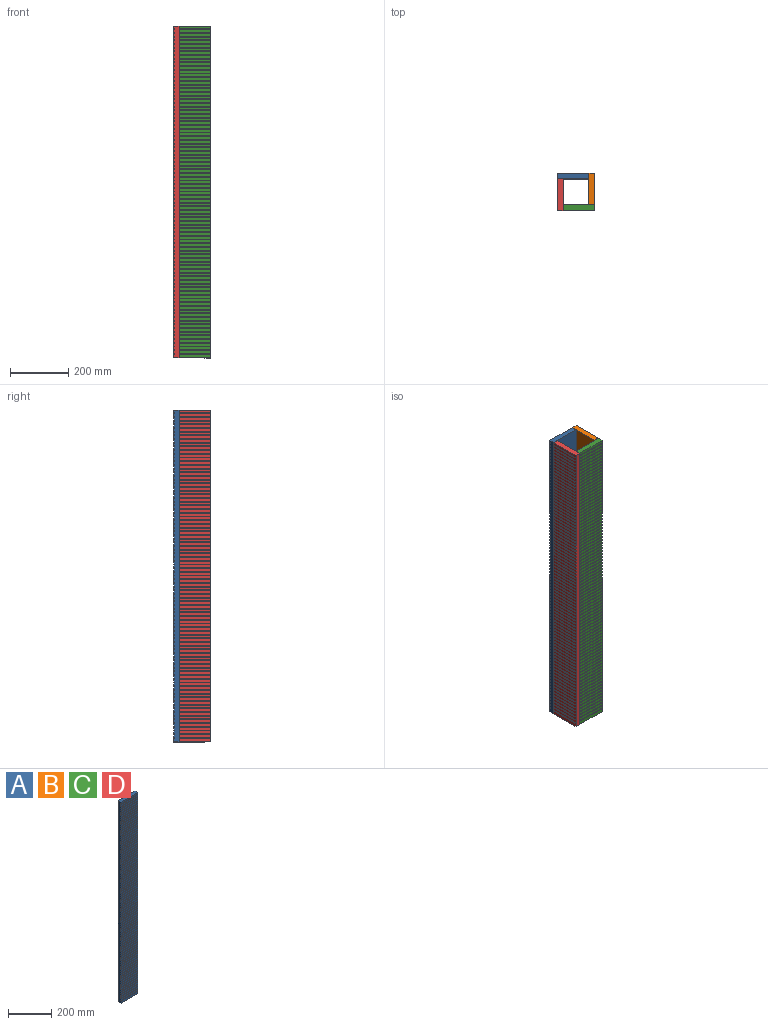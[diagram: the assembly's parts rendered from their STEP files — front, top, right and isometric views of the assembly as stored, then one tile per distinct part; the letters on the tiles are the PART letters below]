
ASSEMBLY  parts=4 mates=3
PART A: 362 faces, bbox 108x19.1x1143 mm
  f0: plane 1143x19.05mm, normal (-1,0,0), area 21325.6mm2, adj f1,f2,f3,f4,f5,f6,f7,f8
  f1: plane 107.95x9.53mm, normal (0,-1,0), area 1028.2mm2, adj f0,f90,f93,f359
  f2: plane 107.95x9.53mm, normal (0,-1,0), area 1028.2mm2, adj f0,f90,f356,f360
  f3: plane 107.95x9.53mm, normal (0,-1,0), area 1028.2mm2, adj f0,f90,f353,f357
  f4: plane 107.95x9.53mm, normal (0,-1,0), area 1028.2mm2, adj f0,f90,f350,f354
  f5: plane 107.95x9.53mm, normal (0,-1,0), area 1028.2mm2, adj f0,f90,f347,f351
  f6: plane 107.95x9.53mm, normal (0,-1,0), area 1028.2mm2, adj f0,f90,f344,f348
  f7: plane 107.95x9.53mm, normal (0,-1,0), area 1028.2mm2, adj f0,f90,f341,f345
  f8: plane 107.95x9.53mm, normal (0,-1,0), area 1028.2mm2, adj f0,f90,f338,f342
  f9: plane 107.95x9.53mm, normal (0,-1,0), area 1028.2mm2, adj f0,f90,f335,f339
  f10: plane 107.95x9.53mm, normal (0,-1,0), area 1028.2mm2, adj f0,f90,f332,f336
  f11: plane 107.95x9.53mm, normal (0,-1,0), area 1028.2mm2, adj f0,f90,f329,f333
  f12: plane 107.95x9.53mm, normal (0,-1,0), area 1028.2mm2, adj f0,f90,f326,f330
  f13: plane 107.95x9.53mm, normal (0,-1,0), area 1028.2mm2, adj f0,f90,f323,f327
  f14: plane 107.95x9.53mm, normal (0,-1,0), area 1028.2mm2, adj f0,f90,f320,f324
  f15: plane 107.95x9.53mm, normal (0,-1,0), area 1028.2mm2, adj f0,f90,f317,f321
  f16: plane 107.95x9.53mm, normal (0,-1,0), area 1028.2mm2, adj f0,f90,f314,f318
  f17: plane 107.95x9.53mm, normal (0,-1,0), area 1028.2mm2, adj f0,f90,f311,f315
  f18: plane 107.95x9.53mm, normal (0,-1,0), area 1028.2mm2, adj f0,f90,f308,f312
  f19: plane 107.95x9.53mm, normal (0,-1,0), area 1028.2mm2, adj f0,f90,f305,f309
  f20: plane 107.95x9.53mm, normal (0,-1,0), area 1028.2mm2, adj f0,f90,f302,f306
  f21: plane 107.95x9.53mm, normal (0,-1,0), area 1028.2mm2, adj f0,f90,f299,f303
  f22: plane 107.95x9.53mm, normal (0,-1,0), area 1028.2mm2, adj f0,f90,f296,f300
  f23: plane 107.95x9.53mm, normal (0,-1,0), area 1028.2mm2, adj f0,f90,f293,f297
  f24: plane 107.95x9.53mm, normal (0,-1,0), area 1028.2mm2, adj f0,f90,f290,f294
  f25: plane 107.95x9.53mm, normal (0,-1,0), area 1028.2mm2, adj f0,f90,f287,f291
  f26: plane 107.95x9.53mm, normal (0,-1,0), area 1028.2mm2, adj f0,f90,f284,f288
  f27: plane 107.95x9.53mm, normal (0,-1,0), area 1028.2mm2, adj f0,f90,f281,f285
  f28: plane 107.95x9.53mm, normal (0,-1,0), area 1028.2mm2, adj f0,f90,f278,f282
  f29: plane 107.95x9.53mm, normal (0,-1,0), area 1028.2mm2, adj f0,f90,f275,f279
  f30: plane 107.95x9.53mm, normal (0,-1,0), area 1028.2mm2, adj f0,f90,f272,f276
  f31: plane 107.95x9.53mm, normal (0,-1,0), area 1028.2mm2, adj f0,f90,f269,f273
  f32: plane 107.95x9.53mm, normal (0,-1,0), area 1028.2mm2, adj f0,f90,f266,f270
  f33: plane 107.95x9.53mm, normal (0,-1,0), area 1028.2mm2, adj f0,f90,f263,f267
  f34: plane 107.95x9.53mm, normal (0,-1,0), area 1028.2mm2, adj f0,f90,f260,f264
  f35: plane 107.95x9.53mm, normal (0,-1,0), area 1028.2mm2, adj f0,f90,f257,f261
  f36: plane 107.95x9.53mm, normal (0,-1,0), area 1028.2mm2, adj f0,f90,f254,f258
  f37: plane 107.95x9.53mm, normal (0,-1,0), area 1028.2mm2, adj f0,f90,f251,f255
  f38: plane 107.95x9.53mm, normal (0,-1,0), area 1028.2mm2, adj f0,f90,f248,f252
  f39: plane 107.95x9.53mm, normal (0,-1,0), area 1028.2mm2, adj f0,f90,f245,f249
  f40: plane 107.95x9.53mm, normal (0,-1,0), area 1028.2mm2, adj f0,f90,f242,f246
  f41: plane 107.95x9.53mm, normal (0,-1,0), area 1028.2mm2, adj f0,f90,f239,f243
  f42: plane 107.95x9.53mm, normal (0,-1,0), area 1028.2mm2, adj f0,f90,f236,f240
  f43: plane 107.95x9.53mm, normal (0,-1,0), area 1028.2mm2, adj f0,f90,f233,f237
  f44: plane 107.95x9.53mm, normal (0,-1,0), area 1028.2mm2, adj f0,f90,f230,f234
  f45: plane 107.95x9.53mm, normal (0,-1,0), area 1028.2mm2, adj f0,f90,f227,f231
  f46: plane 107.95x9.53mm, normal (0,-1,0), area 1028.2mm2, adj f0,f90,f224,f228
  f47: plane 107.95x9.53mm, normal (0,-1,0), area 1028.2mm2, adj f0,f90,f221,f225
  f48: plane 107.95x9.53mm, normal (0,-1,0), area 1028.2mm2, adj f0,f90,f218,f222
  f49: plane 107.95x9.53mm, normal (0,-1,0), area 1028.2mm2, adj f0,f90,f215,f219
  f50: plane 107.95x9.53mm, normal (0,-1,0), area 1028.2mm2, adj f0,f90,f212,f216
  f51: plane 107.95x9.53mm, normal (0,-1,0), area 1028.2mm2, adj f0,f90,f209,f213
  f52: plane 107.95x9.53mm, normal (0,-1,0), area 1028.2mm2, adj f0,f90,f206,f210
  f53: plane 107.95x9.53mm, normal (0,-1,0), area 1028.2mm2, adj f0,f90,f203,f207
  f54: plane 107.95x9.53mm, normal (0,-1,0), area 1028.2mm2, adj f0,f90,f200,f204
  f55: plane 107.95x9.53mm, normal (0,-1,0), area 1028.2mm2, adj f0,f90,f197,f201
  f56: plane 107.95x9.53mm, normal (0,-1,0), area 1028.2mm2, adj f0,f90,f194,f198
  f57: plane 107.95x9.53mm, normal (0,-1,0), area 1028.2mm2, adj f0,f90,f191,f195
  f58: plane 107.95x9.53mm, normal (0,-1,0), area 1028.2mm2, adj f0,f90,f188,f192
  f59: plane 107.95x9.53mm, normal (0,-1,0), area 1028.2mm2, adj f0,f90,f185,f189
  f60: plane 107.95x9.53mm, normal (0,-1,0), area 1028.2mm2, adj f0,f90,f182,f186
  f61: plane 107.95x9.53mm, normal (0,-1,0), area 1028.2mm2, adj f0,f90,f179,f183
  f62: plane 107.95x9.53mm, normal (0,-1,0), area 1028.2mm2, adj f0,f90,f176,f180
  f63: plane 107.95x9.53mm, normal (0,-1,0), area 1028.2mm2, adj f0,f90,f173,f177
  f64: plane 107.95x9.53mm, normal (0,-1,0), area 1028.2mm2, adj f0,f90,f170,f174
  f65: plane 107.95x9.53mm, normal (0,-1,0), area 1028.2mm2, adj f0,f90,f167,f171
  f66: plane 107.95x9.53mm, normal (0,-1,0), area 1028.2mm2, adj f0,f90,f164,f168
  f67: plane 107.95x9.53mm, normal (0,-1,0), area 1028.2mm2, adj f0,f90,f161,f165
  f68: plane 107.95x9.53mm, normal (0,-1,0), area 1028.2mm2, adj f0,f90,f158,f162
  f69: plane 107.95x9.53mm, normal (0,-1,0), area 1028.2mm2, adj f0,f90,f155,f159
  f70: plane 107.95x9.53mm, normal (0,-1,0), area 1028.2mm2, adj f0,f90,f152,f156
  f71: plane 107.95x9.53mm, normal (0,-1,0), area 1028.2mm2, adj f0,f90,f149,f153
  f72: plane 107.95x9.53mm, normal (0,-1,0), area 1028.2mm2, adj f0,f90,f146,f150
  f73: plane 107.95x9.53mm, normal (0,-1,0), area 1028.2mm2, adj f0,f90,f143,f147
  f74: plane 107.95x9.53mm, normal (0,-1,0), area 1028.2mm2, adj f0,f90,f140,f144
  f75: plane 107.95x9.53mm, normal (0,-1,0), area 1028.2mm2, adj f0,f90,f137,f141
  f76: plane 107.95x9.53mm, normal (0,-1,0), area 1028.2mm2, adj f0,f90,f134,f138
  f77: plane 107.95x9.53mm, normal (0,-1,0), area 1028.2mm2, adj f0,f90,f131,f135
  f78: plane 107.95x9.53mm, normal (0,-1,0), area 1028.2mm2, adj f0,f90,f128,f132
  f79: plane 107.95x9.53mm, normal (0,-1,0), area 1028.2mm2, adj f0,f90,f125,f129
  f80: plane 107.95x9.53mm, normal (0,-1,0), area 1028.2mm2, adj f0,f90,f122,f126
  f81: plane 107.95x9.53mm, normal (0,-1,0), area 1028.2mm2, adj f0,f90,f119,f123
  f82: plane 107.95x9.53mm, normal (0,-1,0), area 1028.2mm2, adj f0,f90,f116,f120
  f83: plane 107.95x9.53mm, normal (0,-1,0), area 1028.2mm2, adj f0,f90,f113,f117
  f84: plane 107.95x9.53mm, normal (0,-1,0), area 1028.2mm2, adj f0,f90,f110,f114
  f85: plane 107.95x9.53mm, normal (0,-1,0), area 1028.2mm2, adj f0,f90,f107,f111
  f86: plane 107.95x9.53mm, normal (0,-1,0), area 1028.2mm2, adj f0,f90,f104,f108
  f87: plane 107.95x9.53mm, normal (0,-1,0), area 1028.2mm2, adj f0,f90,f101,f105
  f88: plane 107.95x9.53mm, normal (0,-1,0), area 1028.2mm2, adj f0,f90,f98,f102
  f89: plane 107.95x9.53mm, normal (0,-1,0), area 1028.2mm2, adj f0,f90,f95,f99
  f90: plane 1143x19.05mm, normal (1,0,0), area 21325.6mm2, adj f1,f2,f3,f4,f5,f6,f7,f8
  f91: plane 1143x107.95mm, normal (0,1,0), area 123386.8mm2, adj f0,f90,f93,f94
  f92: plane 107.95x12.7mm, normal (0,-1,0), area 1371mm2, adj f0,f90,f94,f96
  f93: plane 107.95x19.05mm, normal (0,0,1), area 2056.4mm2, adj f0,f1,f90,f91
  f94: plane 107.95x19.05mm, normal (0,0,-1), area 2056.4mm2, adj f0,f90,f91,f92
  f95: plane 107.95x1.59mm, normal (0,0,-1), area 171.4mm2, adj f0,f89,f90,f97
  f96: plane 107.95x1.59mm, normal (0,0,1), area 171.4mm2, adj f0,f90,f92,f97
  f97: plane 107.95x3.18mm, normal (0,-1,0), area 342.7mm2, adj f0,f90,f95,f96
  f98: plane 107.95x1.59mm, normal (0,0,-1), area 171.4mm2, adj f0,f88,f90,f100
  f99: plane 107.95x1.59mm, normal (0,0,1), area 171.4mm2, adj f0,f89,f90,f100
  f100: plane 107.95x3.18mm, normal (0,-1,0), area 342.7mm2, adj f0,f90,f98,f99
  f101: plane 107.95x1.59mm, normal (0,0,-1), area 171.4mm2, adj f0,f87,f90,f103
  f102: plane 107.95x1.59mm, normal (0,0,1), area 171.4mm2, adj f0,f88,f90,f103
  f103: plane 107.95x3.18mm, normal (0,-1,0), area 342.7mm2, adj f0,f90,f101,f102
  f104: plane 107.95x1.59mm, normal (0,0,-1), area 171.4mm2, adj f0,f86,f90,f106
  f105: plane 107.95x1.59mm, normal (0,0,1), area 171.4mm2, adj f0,f87,f90,f106
  f106: plane 107.95x3.18mm, normal (0,-1,0), area 342.7mm2, adj f0,f90,f104,f105
  f107: plane 107.95x1.59mm, normal (0,0,-1), area 171.4mm2, adj f0,f85,f90,f109
  f108: plane 107.95x1.59mm, normal (0,0,1), area 171.4mm2, adj f0,f86,f90,f109
  f109: plane 107.95x3.18mm, normal (0,-1,0), area 342.7mm2, adj f0,f90,f107,f108
  f110: plane 107.95x1.59mm, normal (0,0,-1), area 171.4mm2, adj f0,f84,f90,f112
  f111: plane 107.95x1.59mm, normal (0,0,1), area 171.4mm2, adj f0,f85,f90,f112
  f112: plane 107.95x3.18mm, normal (0,-1,0), area 342.7mm2, adj f0,f90,f110,f111
  f113: plane 107.95x1.59mm, normal (0,0,-1), area 171.4mm2, adj f0,f83,f90,f115
  f114: plane 107.95x1.59mm, normal (0,0,1), area 171.4mm2, adj f0,f84,f90,f115
  f115: plane 107.95x3.18mm, normal (0,-1,0), area 342.7mm2, adj f0,f90,f113,f114
  f116: plane 107.95x1.59mm, normal (0,0,-1), area 171.4mm2, adj f0,f82,f90,f118
  f117: plane 107.95x1.59mm, normal (0,0,1), area 171.4mm2, adj f0,f83,f90,f118
  f118: plane 107.95x3.18mm, normal (0,-1,0), area 342.7mm2, adj f0,f90,f116,f117
  f119: plane 107.95x1.59mm, normal (0,0,-1), area 171.4mm2, adj f0,f81,f90,f121
  f120: plane 107.95x1.59mm, normal (0,0,1), area 171.4mm2, adj f0,f82,f90,f121
  f121: plane 107.95x3.18mm, normal (0,-1,0), area 342.7mm2, adj f0,f90,f119,f120
  f122: plane 107.95x1.59mm, normal (0,0,-1), area 171.4mm2, adj f0,f80,f90,f124
  f123: plane 107.95x1.59mm, normal (0,0,1), area 171.4mm2, adj f0,f81,f90,f124
  f124: plane 107.95x3.18mm, normal (0,-1,0), area 342.7mm2, adj f0,f90,f122,f123
  f125: plane 107.95x1.59mm, normal (0,0,-1), area 171.4mm2, adj f0,f79,f90,f127
  f126: plane 107.95x1.59mm, normal (0,0,1), area 171.4mm2, adj f0,f80,f90,f127
  f127: plane 107.95x3.18mm, normal (0,-1,0), area 342.7mm2, adj f0,f90,f125,f126
  f128: plane 107.95x1.59mm, normal (0,0,-1), area 171.4mm2, adj f0,f78,f90,f130
  f129: plane 107.95x1.59mm, normal (0,0,1), area 171.4mm2, adj f0,f79,f90,f130
  f130: plane 107.95x3.18mm, normal (0,-1,0), area 342.7mm2, adj f0,f90,f128,f129
  f131: plane 107.95x1.59mm, normal (0,0,-1), area 171.4mm2, adj f0,f77,f90,f133
  f132: plane 107.95x1.59mm, normal (0,0,1), area 171.4mm2, adj f0,f78,f90,f133
  f133: plane 107.95x3.18mm, normal (0,-1,0), area 342.7mm2, adj f0,f90,f131,f132
  f134: plane 107.95x1.59mm, normal (0,0,-1), area 171.4mm2, adj f0,f76,f90,f136
  f135: plane 107.95x1.59mm, normal (0,0,1), area 171.4mm2, adj f0,f77,f90,f136
  f136: plane 107.95x3.18mm, normal (0,-1,0), area 342.7mm2, adj f0,f90,f134,f135
  f137: plane 107.95x1.59mm, normal (0,0,-1), area 171.4mm2, adj f0,f75,f90,f139
  f138: plane 107.95x1.59mm, normal (0,0,1), area 171.4mm2, adj f0,f76,f90,f139
  f139: plane 107.95x3.18mm, normal (0,-1,0), area 342.7mm2, adj f0,f90,f137,f138
  f140: plane 107.95x1.59mm, normal (0,0,-1), area 171.4mm2, adj f0,f74,f90,f142
  f141: plane 107.95x1.59mm, normal (0,0,1), area 171.4mm2, adj f0,f75,f90,f142
  f142: plane 107.95x3.18mm, normal (0,-1,0), area 342.7mm2, adj f0,f90,f140,f141
  f143: plane 107.95x1.59mm, normal (0,0,-1), area 171.4mm2, adj f0,f73,f90,f145
  f144: plane 107.95x1.59mm, normal (0,0,1), area 171.4mm2, adj f0,f74,f90,f145
  f145: plane 107.95x3.18mm, normal (0,-1,0), area 342.7mm2, adj f0,f90,f143,f144
  f146: plane 107.95x1.59mm, normal (0,0,-1), area 171.4mm2, adj f0,f72,f90,f148
  f147: plane 107.95x1.59mm, normal (0,0,1), area 171.4mm2, adj f0,f73,f90,f148
  f148: plane 107.95x3.18mm, normal (0,-1,0), area 342.7mm2, adj f0,f90,f146,f147
  f149: plane 107.95x1.59mm, normal (0,0,-1), area 171.4mm2, adj f0,f71,f90,f151
  f150: plane 107.95x1.59mm, normal (0,0,1), area 171.4mm2, adj f0,f72,f90,f151
  f151: plane 107.95x3.18mm, normal (0,-1,0), area 342.7mm2, adj f0,f90,f149,f150
  f152: plane 107.95x1.59mm, normal (0,0,-1), area 171.4mm2, adj f0,f70,f90,f154
  f153: plane 107.95x1.59mm, normal (0,0,1), area 171.4mm2, adj f0,f71,f90,f154
  f154: plane 107.95x3.18mm, normal (0,-1,0), area 342.7mm2, adj f0,f90,f152,f153
  f155: plane 107.95x1.59mm, normal (0,0,-1), area 171.4mm2, adj f0,f69,f90,f157
  f156: plane 107.95x1.59mm, normal (0,0,1), area 171.4mm2, adj f0,f70,f90,f157
  f157: plane 107.95x3.18mm, normal (0,-1,0), area 342.7mm2, adj f0,f90,f155,f156
  f158: plane 107.95x1.59mm, normal (0,0,-1), area 171.4mm2, adj f0,f68,f90,f160
  f159: plane 107.95x1.59mm, normal (0,0,1), area 171.4mm2, adj f0,f69,f90,f160
  f160: plane 107.95x3.18mm, normal (0,-1,0), area 342.7mm2, adj f0,f90,f158,f159
  f161: plane 107.95x1.59mm, normal (0,0,-1), area 171.4mm2, adj f0,f67,f90,f163
  f162: plane 107.95x1.59mm, normal (0,0,1), area 171.4mm2, adj f0,f68,f90,f163
  f163: plane 107.95x3.18mm, normal (0,-1,0), area 342.7mm2, adj f0,f90,f161,f162
  f164: plane 107.95x1.59mm, normal (0,0,-1), area 171.4mm2, adj f0,f66,f90,f166
  f165: plane 107.95x1.59mm, normal (0,0,1), area 171.4mm2, adj f0,f67,f90,f166
  f166: plane 107.95x3.18mm, normal (0,-1,0), area 342.7mm2, adj f0,f90,f164,f165
  f167: plane 107.95x1.59mm, normal (0,0,-1), area 171.4mm2, adj f0,f65,f90,f169
  f168: plane 107.95x1.59mm, normal (0,0,1), area 171.4mm2, adj f0,f66,f90,f169
  f169: plane 107.95x3.18mm, normal (0,-1,0), area 342.7mm2, adj f0,f90,f167,f168
  f170: plane 107.95x1.59mm, normal (0,0,-1), area 171.4mm2, adj f0,f64,f90,f172
  f171: plane 107.95x1.59mm, normal (0,0,1), area 171.4mm2, adj f0,f65,f90,f172
  f172: plane 107.95x3.18mm, normal (0,-1,0), area 342.7mm2, adj f0,f90,f170,f171
  f173: plane 107.95x1.59mm, normal (0,0,-1), area 171.4mm2, adj f0,f63,f90,f175
  f174: plane 107.95x1.59mm, normal (0,0,1), area 171.4mm2, adj f0,f64,f90,f175
  f175: plane 107.95x3.18mm, normal (0,-1,0), area 342.7mm2, adj f0,f90,f173,f174
  f176: plane 107.95x1.59mm, normal (0,0,-1), area 171.4mm2, adj f0,f62,f90,f178
  f177: plane 107.95x1.59mm, normal (0,0,1), area 171.4mm2, adj f0,f63,f90,f178
  f178: plane 107.95x3.18mm, normal (0,-1,0), area 342.7mm2, adj f0,f90,f176,f177
  f179: plane 107.95x1.59mm, normal (0,0,-1), area 171.4mm2, adj f0,f61,f90,f181
  f180: plane 107.95x1.59mm, normal (0,0,1), area 171.4mm2, adj f0,f62,f90,f181
  f181: plane 107.95x3.18mm, normal (0,-1,0), area 342.7mm2, adj f0,f90,f179,f180
  f182: plane 107.95x1.59mm, normal (0,0,-1), area 171.4mm2, adj f0,f60,f90,f184
  f183: plane 107.95x1.59mm, normal (0,0,1), area 171.4mm2, adj f0,f61,f90,f184
  f184: plane 107.95x3.18mm, normal (0,-1,0), area 342.7mm2, adj f0,f90,f182,f183
  f185: plane 107.95x1.59mm, normal (0,0,-1), area 171.4mm2, adj f0,f59,f90,f187
  f186: plane 107.95x1.59mm, normal (0,0,1), area 171.4mm2, adj f0,f60,f90,f187
  f187: plane 107.95x3.18mm, normal (0,-1,0), area 342.7mm2, adj f0,f90,f185,f186
  f188: plane 107.95x1.59mm, normal (0,0,-1), area 171.4mm2, adj f0,f58,f90,f190
  f189: plane 107.95x1.59mm, normal (0,0,1), area 171.4mm2, adj f0,f59,f90,f190
  f190: plane 107.95x3.18mm, normal (0,-1,0), area 342.7mm2, adj f0,f90,f188,f189
  f191: plane 107.95x1.59mm, normal (0,0,-1), area 171.4mm2, adj f0,f57,f90,f193
  f192: plane 107.95x1.59mm, normal (0,0,1), area 171.4mm2, adj f0,f58,f90,f193
  f193: plane 107.95x3.18mm, normal (0,-1,0), area 342.7mm2, adj f0,f90,f191,f192
  f194: plane 107.95x1.59mm, normal (0,0,-1), area 171.4mm2, adj f0,f56,f90,f196
  f195: plane 107.95x1.59mm, normal (0,0,1), area 171.4mm2, adj f0,f57,f90,f196
  f196: plane 107.95x3.18mm, normal (0,-1,0), area 342.7mm2, adj f0,f90,f194,f195
  f197: plane 107.95x1.59mm, normal (0,0,-1), area 171.4mm2, adj f0,f55,f90,f199
  f198: plane 107.95x1.59mm, normal (0,0,1), area 171.4mm2, adj f0,f56,f90,f199
  f199: plane 107.95x3.18mm, normal (0,-1,0), area 342.7mm2, adj f0,f90,f197,f198
  f200: plane 107.95x1.59mm, normal (0,0,-1), area 171.4mm2, adj f0,f54,f90,f202
  f201: plane 107.95x1.59mm, normal (0,0,1), area 171.4mm2, adj f0,f55,f90,f202
  f202: plane 107.95x3.18mm, normal (0,-1,0), area 342.7mm2, adj f0,f90,f200,f201
  f203: plane 107.95x1.59mm, normal (0,0,-1), area 171.4mm2, adj f0,f53,f90,f205
  f204: plane 107.95x1.59mm, normal (0,0,1), area 171.4mm2, adj f0,f54,f90,f205
  f205: plane 107.95x3.18mm, normal (0,-1,0), area 342.7mm2, adj f0,f90,f203,f204
  f206: plane 107.95x1.59mm, normal (0,0,-1), area 171.4mm2, adj f0,f52,f90,f208
  f207: plane 107.95x1.59mm, normal (0,0,1), area 171.4mm2, adj f0,f53,f90,f208
  f208: plane 107.95x3.18mm, normal (0,-1,0), area 342.7mm2, adj f0,f90,f206,f207
  f209: plane 107.95x1.59mm, normal (0,0,-1), area 171.4mm2, adj f0,f51,f90,f211
  f210: plane 107.95x1.59mm, normal (0,0,1), area 171.4mm2, adj f0,f52,f90,f211
  f211: plane 107.95x3.18mm, normal (0,-1,0), area 342.7mm2, adj f0,f90,f209,f210
  f212: plane 107.95x1.59mm, normal (0,0,-1), area 171.4mm2, adj f0,f50,f90,f214
  f213: plane 107.95x1.59mm, normal (0,0,1), area 171.4mm2, adj f0,f51,f90,f214
  f214: plane 107.95x3.18mm, normal (0,-1,0), area 342.7mm2, adj f0,f90,f212,f213
  f215: plane 107.95x1.59mm, normal (0,0,-1), area 171.4mm2, adj f0,f49,f90,f217
  f216: plane 107.95x1.59mm, normal (0,0,1), area 171.4mm2, adj f0,f50,f90,f217
  f217: plane 107.95x3.18mm, normal (0,-1,0), area 342.7mm2, adj f0,f90,f215,f216
  f218: plane 107.95x1.59mm, normal (0,0,-1), area 171.4mm2, adj f0,f48,f90,f220
  f219: plane 107.95x1.59mm, normal (0,0,1), area 171.4mm2, adj f0,f49,f90,f220
  f220: plane 107.95x3.18mm, normal (0,-1,0), area 342.7mm2, adj f0,f90,f218,f219
  f221: plane 107.95x1.59mm, normal (0,0,-1), area 171.4mm2, adj f0,f47,f90,f223
  f222: plane 107.95x1.59mm, normal (0,0,1), area 171.4mm2, adj f0,f48,f90,f223
  f223: plane 107.95x3.18mm, normal (0,-1,0), area 342.7mm2, adj f0,f90,f221,f222
  f224: plane 107.95x1.59mm, normal (0,0,-1), area 171.4mm2, adj f0,f46,f90,f226
  f225: plane 107.95x1.59mm, normal (0,0,1), area 171.4mm2, adj f0,f47,f90,f226
  f226: plane 107.95x3.18mm, normal (0,-1,0), area 342.7mm2, adj f0,f90,f224,f225
  f227: plane 107.95x1.59mm, normal (0,0,-1), area 171.4mm2, adj f0,f45,f90,f229
  f228: plane 107.95x1.59mm, normal (0,0,1), area 171.4mm2, adj f0,f46,f90,f229
  f229: plane 107.95x3.18mm, normal (0,-1,0), area 342.7mm2, adj f0,f90,f227,f228
  f230: plane 107.95x1.59mm, normal (0,0,-1), area 171.4mm2, adj f0,f44,f90,f232
  f231: plane 107.95x1.59mm, normal (0,0,1), area 171.4mm2, adj f0,f45,f90,f232
  f232: plane 107.95x3.18mm, normal (0,-1,0), area 342.7mm2, adj f0,f90,f230,f231
  f233: plane 107.95x1.59mm, normal (0,0,-1), area 171.4mm2, adj f0,f43,f90,f235
  f234: plane 107.95x1.59mm, normal (0,0,1), area 171.4mm2, adj f0,f44,f90,f235
  f235: plane 107.95x3.18mm, normal (0,-1,0), area 342.7mm2, adj f0,f90,f233,f234
  f236: plane 107.95x1.59mm, normal (0,0,-1), area 171.4mm2, adj f0,f42,f90,f238
  f237: plane 107.95x1.59mm, normal (0,0,1), area 171.4mm2, adj f0,f43,f90,f238
  f238: plane 107.95x3.18mm, normal (0,-1,0), area 342.7mm2, adj f0,f90,f236,f237
  f239: plane 107.95x1.59mm, normal (0,0,-1), area 171.4mm2, adj f0,f41,f90,f241
  f240: plane 107.95x1.59mm, normal (0,0,1), area 171.4mm2, adj f0,f42,f90,f241
  f241: plane 107.95x3.18mm, normal (0,-1,0), area 342.7mm2, adj f0,f90,f239,f240
  f242: plane 107.95x1.59mm, normal (0,0,-1), area 171.4mm2, adj f0,f40,f90,f244
  f243: plane 107.95x1.59mm, normal (0,0,1), area 171.4mm2, adj f0,f41,f90,f244
  f244: plane 107.95x3.18mm, normal (0,-1,0), area 342.7mm2, adj f0,f90,f242,f243
  f245: plane 107.95x1.59mm, normal (0,0,-1), area 171.4mm2, adj f0,f39,f90,f247
  f246: plane 107.95x1.59mm, normal (0,0,1), area 171.4mm2, adj f0,f40,f90,f247
  f247: plane 107.95x3.18mm, normal (0,-1,0), area 342.7mm2, adj f0,f90,f245,f246
  f248: plane 107.95x1.59mm, normal (0,0,-1), area 171.4mm2, adj f0,f38,f90,f250
  f249: plane 107.95x1.59mm, normal (0,0,1), area 171.4mm2, adj f0,f39,f90,f250
  f250: plane 107.95x3.18mm, normal (0,-1,0), area 342.7mm2, adj f0,f90,f248,f249
  f251: plane 107.95x1.59mm, normal (0,0,-1), area 171.4mm2, adj f0,f37,f90,f253
  f252: plane 107.95x1.59mm, normal (0,0,1), area 171.4mm2, adj f0,f38,f90,f253
  f253: plane 107.95x3.18mm, normal (0,-1,0), area 342.7mm2, adj f0,f90,f251,f252
  f254: plane 107.95x1.59mm, normal (0,0,-1), area 171.4mm2, adj f0,f36,f90,f256
  f255: plane 107.95x1.59mm, normal (0,0,1), area 171.4mm2, adj f0,f37,f90,f256
  f256: plane 107.95x3.18mm, normal (0,-1,0), area 342.7mm2, adj f0,f90,f254,f255
  f257: plane 107.95x1.59mm, normal (0,0,-1), area 171.4mm2, adj f0,f35,f90,f259
  f258: plane 107.95x1.59mm, normal (0,0,1), area 171.4mm2, adj f0,f36,f90,f259
  f259: plane 107.95x3.18mm, normal (0,-1,0), area 342.7mm2, adj f0,f90,f257,f258
  f260: plane 107.95x1.59mm, normal (0,0,-1), area 171.4mm2, adj f0,f34,f90,f262
  f261: plane 107.95x1.59mm, normal (0,0,1), area 171.4mm2, adj f0,f35,f90,f262
  f262: plane 107.95x3.18mm, normal (0,-1,0), area 342.7mm2, adj f0,f90,f260,f261
  f263: plane 107.95x1.59mm, normal (0,0,-1), area 171.4mm2, adj f0,f33,f90,f265
  f264: plane 107.95x1.59mm, normal (0,0,1), area 171.4mm2, adj f0,f34,f90,f265
  f265: plane 107.95x3.18mm, normal (0,-1,0), area 342.7mm2, adj f0,f90,f263,f264
  f266: plane 107.95x1.59mm, normal (0,0,-1), area 171.4mm2, adj f0,f32,f90,f268
  f267: plane 107.95x1.59mm, normal (0,0,1), area 171.4mm2, adj f0,f33,f90,f268
  f268: plane 107.95x3.18mm, normal (0,-1,0), area 342.7mm2, adj f0,f90,f266,f267
  f269: plane 107.95x1.59mm, normal (0,0,-1), area 171.4mm2, adj f0,f31,f90,f271
  f270: plane 107.95x1.59mm, normal (0,0,1), area 171.4mm2, adj f0,f32,f90,f271
  f271: plane 107.95x3.18mm, normal (0,-1,0), area 342.7mm2, adj f0,f90,f269,f270
  f272: plane 107.95x1.59mm, normal (0,0,-1), area 171.4mm2, adj f0,f30,f90,f274
  f273: plane 107.95x1.59mm, normal (0,0,1), area 171.4mm2, adj f0,f31,f90,f274
  f274: plane 107.95x3.18mm, normal (0,-1,0), area 342.7mm2, adj f0,f90,f272,f273
  f275: plane 107.95x1.59mm, normal (0,0,-1), area 171.4mm2, adj f0,f29,f90,f277
  f276: plane 107.95x1.59mm, normal (0,0,1), area 171.4mm2, adj f0,f30,f90,f277
  f277: plane 107.95x3.18mm, normal (0,-1,0), area 342.7mm2, adj f0,f90,f275,f276
  f278: plane 107.95x1.59mm, normal (0,0,-1), area 171.4mm2, adj f0,f28,f90,f280
  f279: plane 107.95x1.59mm, normal (0,0,1), area 171.4mm2, adj f0,f29,f90,f280
  f280: plane 107.95x3.18mm, normal (0,-1,0), area 342.7mm2, adj f0,f90,f278,f279
  f281: plane 107.95x1.59mm, normal (0,0,-1), area 171.4mm2, adj f0,f27,f90,f283
  f282: plane 107.95x1.59mm, normal (0,0,1), area 171.4mm2, adj f0,f28,f90,f283
  f283: plane 107.95x3.18mm, normal (0,-1,0), area 342.7mm2, adj f0,f90,f281,f282
  f284: plane 107.95x1.59mm, normal (0,0,-1), area 171.4mm2, adj f0,f26,f90,f286
  f285: plane 107.95x1.59mm, normal (0,0,1), area 171.4mm2, adj f0,f27,f90,f286
  f286: plane 107.95x3.18mm, normal (0,-1,0), area 342.7mm2, adj f0,f90,f284,f285
  f287: plane 107.95x1.59mm, normal (0,0,-1), area 171.4mm2, adj f0,f25,f90,f289
  f288: plane 107.95x1.59mm, normal (0,0,1), area 171.4mm2, adj f0,f26,f90,f289
  f289: plane 107.95x3.18mm, normal (0,-1,0), area 342.7mm2, adj f0,f90,f287,f288
  f290: plane 107.95x1.59mm, normal (0,0,-1), area 171.4mm2, adj f0,f24,f90,f292
  f291: plane 107.95x1.59mm, normal (0,0,1), area 171.4mm2, adj f0,f25,f90,f292
  f292: plane 107.95x3.18mm, normal (0,-1,0), area 342.7mm2, adj f0,f90,f290,f291
  f293: plane 107.95x1.59mm, normal (0,0,-1), area 171.4mm2, adj f0,f23,f90,f295
  f294: plane 107.95x1.59mm, normal (0,0,1), area 171.4mm2, adj f0,f24,f90,f295
  f295: plane 107.95x3.18mm, normal (0,-1,0), area 342.7mm2, adj f0,f90,f293,f294
  f296: plane 107.95x1.59mm, normal (0,0,-1), area 171.4mm2, adj f0,f22,f90,f298
  f297: plane 107.95x1.59mm, normal (0,0,1), area 171.4mm2, adj f0,f23,f90,f298
  f298: plane 107.95x3.18mm, normal (0,-1,0), area 342.7mm2, adj f0,f90,f296,f297
  f299: plane 107.95x1.59mm, normal (0,0,-1), area 171.4mm2, adj f0,f21,f90,f301
  f300: plane 107.95x1.59mm, normal (0,0,1), area 171.4mm2, adj f0,f22,f90,f301
  f301: plane 107.95x3.18mm, normal (0,-1,0), area 342.7mm2, adj f0,f90,f299,f300
  f302: plane 107.95x1.59mm, normal (0,0,-1), area 171.4mm2, adj f0,f20,f90,f304
  f303: plane 107.95x1.59mm, normal (0,0,1), area 171.4mm2, adj f0,f21,f90,f304
  f304: plane 107.95x3.18mm, normal (0,-1,0), area 342.7mm2, adj f0,f90,f302,f303
  f305: plane 107.95x1.59mm, normal (0,0,-1), area 171.4mm2, adj f0,f19,f90,f307
  f306: plane 107.95x1.59mm, normal (0,0,1), area 171.4mm2, adj f0,f20,f90,f307
  f307: plane 107.95x3.18mm, normal (0,-1,0), area 342.7mm2, adj f0,f90,f305,f306
  f308: plane 107.95x1.59mm, normal (0,0,-1), area 171.4mm2, adj f0,f18,f90,f310
  f309: plane 107.95x1.59mm, normal (0,0,1), area 171.4mm2, adj f0,f19,f90,f310
  f310: plane 107.95x3.18mm, normal (0,-1,0), area 342.7mm2, adj f0,f90,f308,f309
  f311: plane 107.95x1.59mm, normal (0,0,-1), area 171.4mm2, adj f0,f17,f90,f313
  f312: plane 107.95x1.59mm, normal (0,0,1), area 171.4mm2, adj f0,f18,f90,f313
  f313: plane 107.95x3.18mm, normal (0,-1,0), area 342.7mm2, adj f0,f90,f311,f312
  f314: plane 107.95x1.59mm, normal (0,0,-1), area 171.4mm2, adj f0,f16,f90,f316
  f315: plane 107.95x1.59mm, normal (0,0,1), area 171.4mm2, adj f0,f17,f90,f316
  f316: plane 107.95x3.18mm, normal (0,-1,0), area 342.7mm2, adj f0,f90,f314,f315
  f317: plane 107.95x1.59mm, normal (0,0,-1), area 171.4mm2, adj f0,f15,f90,f319
  f318: plane 107.95x1.59mm, normal (0,0,1), area 171.4mm2, adj f0,f16,f90,f319
  f319: plane 107.95x3.18mm, normal (0,-1,0), area 342.7mm2, adj f0,f90,f317,f318
  f320: plane 107.95x1.59mm, normal (0,0,-1), area 171.4mm2, adj f0,f14,f90,f322
  f321: plane 107.95x1.59mm, normal (0,0,1), area 171.4mm2, adj f0,f15,f90,f322
  f322: plane 107.95x3.18mm, normal (0,-1,0), area 342.7mm2, adj f0,f90,f320,f321
  f323: plane 107.95x1.59mm, normal (0,0,-1), area 171.4mm2, adj f0,f13,f90,f325
  f324: plane 107.95x1.59mm, normal (0,0,1), area 171.4mm2, adj f0,f14,f90,f325
  f325: plane 107.95x3.18mm, normal (0,-1,0), area 342.7mm2, adj f0,f90,f323,f324
  f326: plane 107.95x1.59mm, normal (0,0,-1), area 171.4mm2, adj f0,f12,f90,f328
  f327: plane 107.95x1.59mm, normal (0,0,1), area 171.4mm2, adj f0,f13,f90,f328
  f328: plane 107.95x3.18mm, normal (0,-1,0), area 342.7mm2, adj f0,f90,f326,f327
  f329: plane 107.95x1.59mm, normal (0,0,-1), area 171.4mm2, adj f0,f11,f90,f331
  f330: plane 107.95x1.59mm, normal (0,0,1), area 171.4mm2, adj f0,f12,f90,f331
  f331: plane 107.95x3.18mm, normal (0,-1,0), area 342.7mm2, adj f0,f90,f329,f330
  f332: plane 107.95x1.59mm, normal (0,0,-1), area 171.4mm2, adj f0,f10,f90,f334
  f333: plane 107.95x1.59mm, normal (0,0,1), area 171.4mm2, adj f0,f11,f90,f334
  f334: plane 107.95x3.18mm, normal (0,-1,0), area 342.7mm2, adj f0,f90,f332,f333
  f335: plane 107.95x1.59mm, normal (0,0,-1), area 171.4mm2, adj f0,f9,f90,f337
  f336: plane 107.95x1.59mm, normal (0,0,1), area 171.4mm2, adj f0,f10,f90,f337
  f337: plane 107.95x3.18mm, normal (0,-1,0), area 342.7mm2, adj f0,f90,f335,f336
  f338: plane 107.95x1.59mm, normal (0,0,-1), area 171.4mm2, adj f0,f8,f90,f340
  f339: plane 107.95x1.59mm, normal (0,0,1), area 171.4mm2, adj f0,f9,f90,f340
  f340: plane 107.95x3.18mm, normal (0,-1,0), area 342.7mm2, adj f0,f90,f338,f339
  f341: plane 107.95x1.59mm, normal (0,0,-1), area 171.4mm2, adj f0,f7,f90,f343
  f342: plane 107.95x1.59mm, normal (0,0,1), area 171.4mm2, adj f0,f8,f90,f343
  f343: plane 107.95x3.18mm, normal (0,-1,0), area 342.7mm2, adj f0,f90,f341,f342
  f344: plane 107.95x1.59mm, normal (0,0,-1), area 171.4mm2, adj f0,f6,f90,f346
  f345: plane 107.95x1.59mm, normal (0,0,1), area 171.4mm2, adj f0,f7,f90,f346
  f346: plane 107.95x3.18mm, normal (0,-1,0), area 342.7mm2, adj f0,f90,f344,f345
  f347: plane 107.95x1.59mm, normal (0,0,-1), area 171.4mm2, adj f0,f5,f90,f349
  f348: plane 107.95x1.59mm, normal (0,0,1), area 171.4mm2, adj f0,f6,f90,f349
  f349: plane 107.95x3.18mm, normal (0,-1,0), area 342.7mm2, adj f0,f90,f347,f348
  f350: plane 107.95x1.59mm, normal (0,0,-1), area 171.4mm2, adj f0,f4,f90,f352
  f351: plane 107.95x1.59mm, normal (0,0,1), area 171.4mm2, adj f0,f5,f90,f352
  f352: plane 107.95x3.18mm, normal (0,-1,0), area 342.7mm2, adj f0,f90,f350,f351
  f353: plane 107.95x1.59mm, normal (0,0,-1), area 171.4mm2, adj f0,f3,f90,f355
  f354: plane 107.95x1.59mm, normal (0,0,1), area 171.4mm2, adj f0,f4,f90,f355
  f355: plane 107.95x3.18mm, normal (0,-1,0), area 342.7mm2, adj f0,f90,f353,f354
  f356: plane 107.95x1.59mm, normal (0,0,-1), area 171.4mm2, adj f0,f2,f90,f358
  f357: plane 107.95x1.59mm, normal (0,0,1), area 171.4mm2, adj f0,f3,f90,f358
  f358: plane 107.95x3.18mm, normal (0,-1,0), area 342.7mm2, adj f0,f90,f356,f357
  f359: plane 107.95x1.59mm, normal (0,0,-1), area 171.4mm2, adj f0,f1,f90,f361
  f360: plane 107.95x1.59mm, normal (0,0,1), area 171.4mm2, adj f0,f2,f90,f361
  f361: plane 107.95x3.18mm, normal (0,-1,0), area 342.7mm2, adj f0,f90,f359,f360
PART B: same geometry as A
PART C: same geometry as A
PART D: same geometry as A
PLACE A rot(axis=(0,0,1),180deg) t=(-19.59,107.13,-0.76)mm
PLACE B rot(axis=(0,0,1),90deg) t=(43.91,62.68,-0.76)mm
PLACE C t=(-0.54,-0.82,-0.76)mm fixed
PLACE D rot(axis=(0,0,-1),90deg) t=(-64.04,43.63,-0.76)mm
MATE fastened B.f0 <-> C.f91  axis (0,-1,0) through (53.43,8.7,570.74)mm
MATE fastened B.f91 <-> A.f0  axis (-1,0,0) through (34.38,116.65,570.74)mm
MATE fastened D.f0 <-> A.f91  axis (0,1,0) through (-73.57,97.6,570.74)mm
